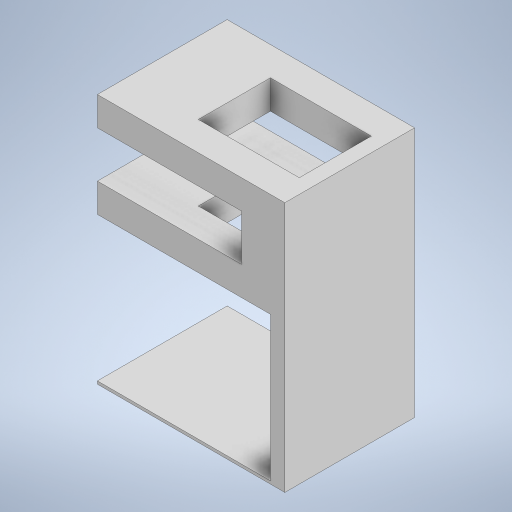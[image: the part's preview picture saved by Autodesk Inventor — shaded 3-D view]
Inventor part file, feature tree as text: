
AUTODESK INVENTOR PART (.ipt)
format: ipt  version: 2023 (Build 270158000, 158)  size: 280,576 bytes
history: native  units: mm
features: extrude x7, sketch x7, other x1
ambient origin geometry x8: Origin, YZ Plane, XZ Plane, XY Plane, X Axis, Y Axis, Z Axis, Center Point
bodies: Body1 (feature_tree)
feature tree (15):
  other  "Твердое тело1"
  extrude  "Выдавливание1"  Depth=60.0mm
  extrude  "Выдавливание3"  Depth=45.0mm
  extrude  "Выдавливание4"  Depth=10.0mm
  extrude  "Выдавливание5"  Depth=35.0mm
  extrude  "Выдавливание6"  Depth=25.0mm
  extrude  "Выдавливание7"  Depth=10.0mm
  extrude  "Выдавливание8"  Depth=10.0mm TaperAngle=0.0deg
  sketch  "Эскиз1"
  sketch  "Эскиз3"
  sketch  "Эскиз4"
  sketch  "Эскиз5"
  sketch  "Эскиз6"
  sketch  "Эскиз7"
  sketch  "Эскиз8"
